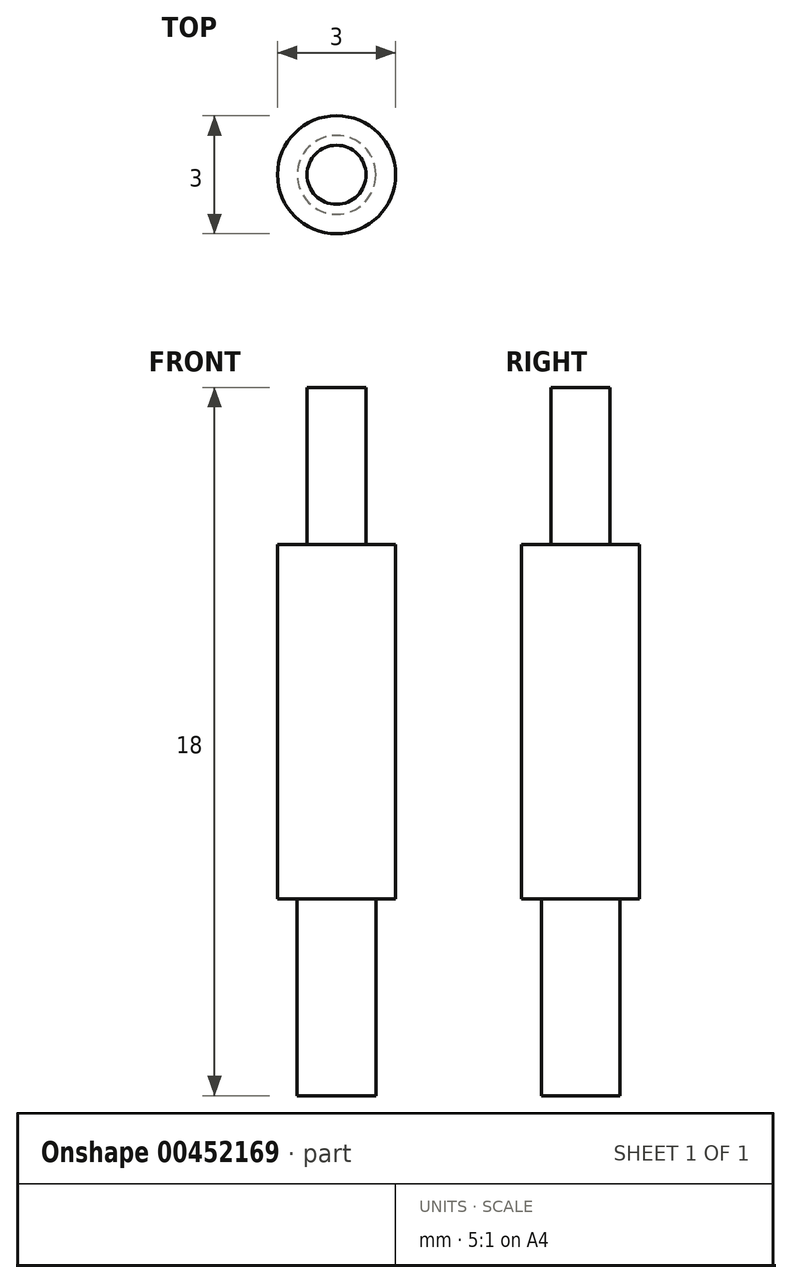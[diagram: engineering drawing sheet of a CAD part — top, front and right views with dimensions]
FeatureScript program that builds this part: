
annotation { "Feature Type Name" : "Feature", "Feature Type Description" : "" }
export const myFeature = defineFeature(function(context is Context, id is Id, definition is map)
    precondition{}
    {
        {
            var Q0;
            Q0=qCreatedBy(makeId("Top.planeOp"),FACE);
            var sketch = newSketch(context, id + "F0", { "sketchPlane" : qUnion([Q0])});
            skCircle(sketch, "E0", {"center": v(0, 0) * mm, "radius": 1.5 * mm});
            skCircle(sketch, "E1", {"center": v(0, 0) * mm, "radius": 1 * mm, "construction": true});
            skSolve(sketch);
        }
        {
            var Q0;
            Q0=makeQuery(id+"F0.imprint","IMPRINT",FACE,{"disambiguationData":[TD([[makeQuery(id+"F0.imprint","IMPRINT",EDGE,{"derivedFrom":sQuery(id+"F0.wireOp",EDGE,"E0")}),1.0]])]});
            extrude(context, id + "F1", {"entities" : qUnion([Q0]), "depth" : 9 * mm});
        }
        {
            var Q0;
            Q0=makeQuery(id+"F1.opExtrude","CAP_FACE",FACE,{"disambiguationData":[OSD([sQuery(id+"F0.wireOp",EDGE,"E0")])],"isStart":false});
            var sketch = newSketch(context, id + "F2", { "sketchPlane" : qUnion([Q0])});
            skCircle(sketch, "E2", {"center": v(0, 0) * mm, "radius": 0.75 * mm});
            skSolve(sketch);
        }
        {
            var Q0;
            Q0 = qSketchRegion(id + "F2", true);
            extrude(context, id + "F3", {"entities" : qUnion([Q0]), "operationType" : NewBodyOperationType.ADD, "depth" : 4 * mm});
        }
        {
            var Q0;
            Q0=qCreatedBy(makeId("Top.planeOp"),FACE);
            var sketch = newSketch(context, id + "F4", { "sketchPlane" : qUnion([Q0])});
            skCircle(sketch, "E3", {"center": v(0, 0) * mm, "radius": 1 * mm});
            skSolve(sketch);
        }
        {
            var Q0;
            Q0=makeQuery(id+"F4.imprint","IMPRINT",FACE,{"disambiguationData":[TD([[makeQuery(id+"F4.imprint","IMPRINT",EDGE,{"derivedFrom":sQuery(id+"F4.wireOp",EDGE,"E3")}),1.0]])]});
            extrude(context, id + "F5", {"entities" : qUnion([Q0]), "operationType" : NewBodyOperationType.ADD, "oppositeDirection" : true, "depth" : 5 * mm});
        }
    });
